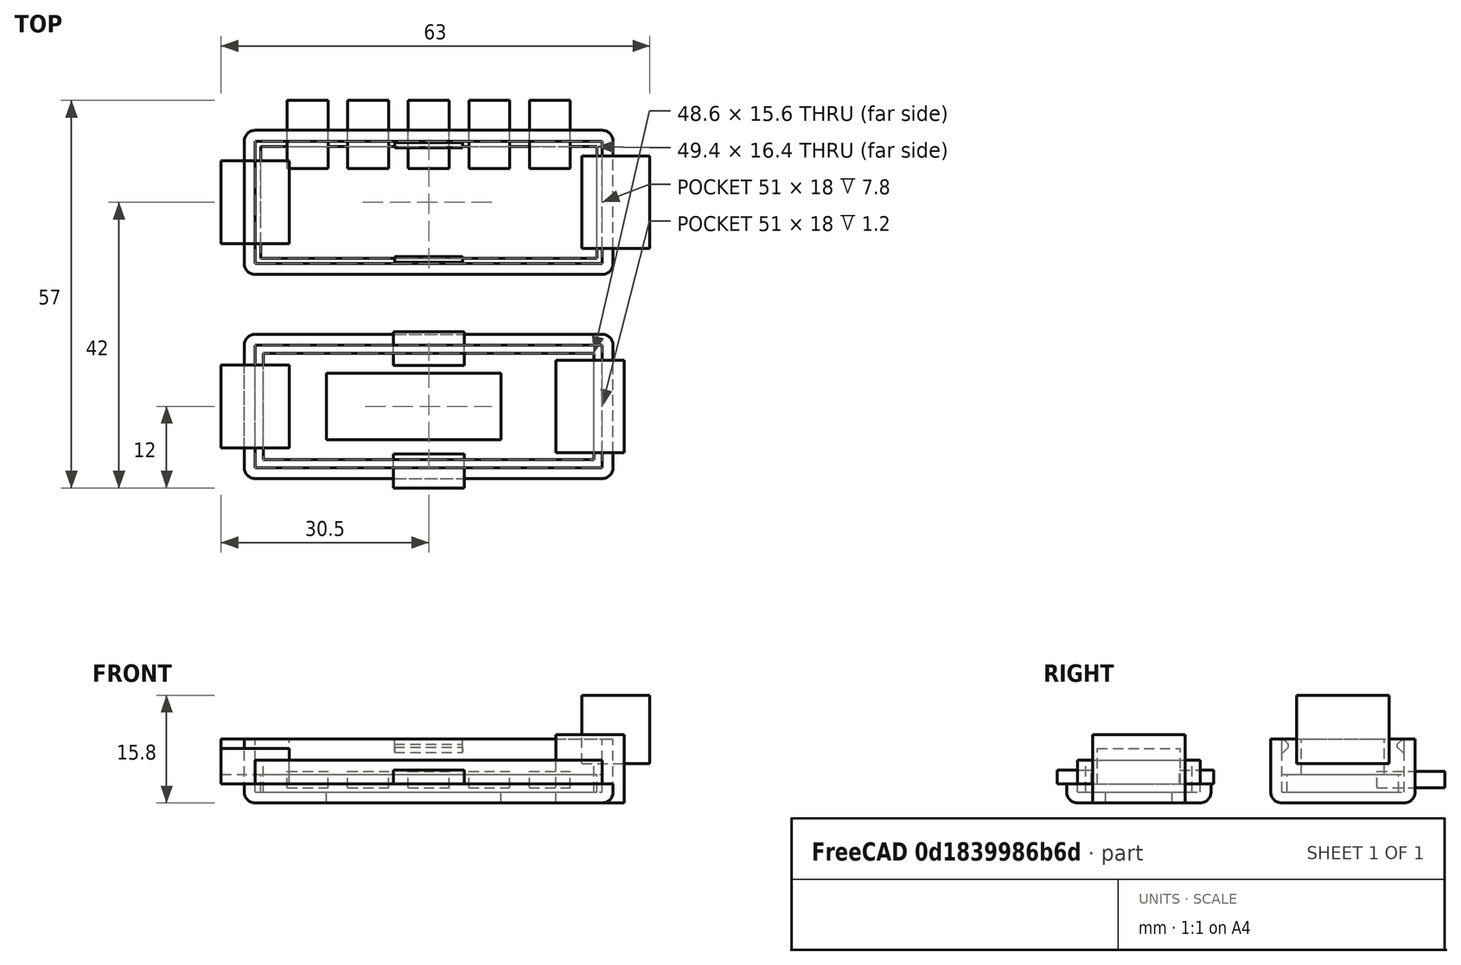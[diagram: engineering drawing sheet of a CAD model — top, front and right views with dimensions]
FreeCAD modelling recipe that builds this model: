
FCSTD DOCUMENT  (FreeCAD 0.16R)
Label: PhoneChargeGuard_raw_v0.1
License: All rights reserved
LicenseURL: http://en.wikipedia.org/wiki/All_rights_reserved
objects: Part::Box×22, Part::Cut×4, Part::Fillet×2, Part::Chamfer×2
note: 30 computed .brp shape members not serialized (recipe doc carries the construction recipe); baked Part::Feature solids carry a one-line shape summary decoded from their .brp

FEATURE [Part::Box] Box  label="unten_außen"
  Height = 9.4
  Length = 54.2
  Placement = pos=(-1.6,-1.6,0) rot=(0,0,1;0rad)
  Width = 21.2
FEATURE [Part::Box] Box001  label="unten_innen"
  Height = 9.4
  Length = 51
  Placement = pos=(0,0,1.6) rot=(0,0,1;0rad)
  Width = 18
FEATURE [Part::Cut] Cut  label="Schale_roh"
  Base = -> Box
  Tool = -> Box001
FEATURE [Part::Fillet] Fillet  label="Schale_unten"
  Base = -> Cut
  Edges = 8 edges r=1.6: [Edge1,Edge3,Edge4,Edge5,Edge6,Edge14,Edge15,Edge16]
FEATURE [Part::Box] Box002  label="Auflage_außen"
  Height = 2.6
  Length = 51
  Placement = pos=(0,0,1.6) rot=(0,0,1;0rad)
  Width = 18
FEATURE [Part::Box] Box003  label="Auflage_innen"
  Height = 2.6
  Length = 49.4
  Placement = pos=(0.8,0.8,1.6) rot=(0,0,1;0rad)
  Width = 16.4
FEATURE [Part::Cut] Cut001  label="Auflage"
  Base = -> Box002
  Tool = -> Box003
FEATURE [Part::Box] Box004  label="Haken1_roh"
  Height = 2
  Length = 10
  Placement = pos=(20.5,0,7.4) rot=(0,0,1;0rad)
  Width = 1
FEATURE [Part::Chamfer] Chamfer  label="Haken1"
  Base = -> Box004
  Edges = 2 edges r=0.8: [Edge11,Edge12]
FEATURE [Part::Box] Box005  label="Haken2_roh"
  Height = 2
  Length = 10
  Placement = pos=(20.5,17,7.4) rot=(0,0,1;0rad)
  Width = 1
FEATURE [Part::Chamfer] Chamfer001  label="Haken2"
  Base = -> Box005
  Edges = 2 edges r=0.8: [Edge9,Edge10]
FEATURE [Part::Box] Box006  label="USB_Stecker"
  Height = 5.2
  Length = 10
  Placement = pos=(-5,2.9,4.2) rot=(0,0,1;0rad)
  Width = 12.2
FEATURE [Part::Box] Box007  label="USB_Buchse"
  Height = 10
  Length = 10
  Placement = pos=(48,2.2,5.8) rot=(0,0,1;0rad)
  Width = 13.6
FEATURE [Part::Box] Box008  label="Button1"
  Height = 2.4
  Length = 6
  Placement = pos=(4.7,14,2.2) rot=(0,0,1;0rad)
  Width = 10
FEATURE [Part::Box] Box009  label="Button2"
  Height = 2.4
  Length = 6
  Placement = pos=(13.6,14,2.2) rot=(0,0,1;0rad)
  Width = 10
FEATURE [Part::Box] Box010  label="oben_außen"
  Height = 2.8
  Length = 54.2
  Placement = pos=(-1.6,-31.6,0) rot=(0,0,1;0rad)
  Width = 21.2
FEATURE [Part::Box] Box011  label="oben_innen"
  Height = 9.4
  Length = 51
  Placement = pos=(0,-30,1.6) rot=(0,0,1;0rad)
  Width = 18
FEATURE [Part::Cut] Cut002  label="Schale_oben_roh"
  Base = -> Box010
  Tool = -> Box011
FEATURE [Part::Fillet] Fillet001  label="Schale_oben"
  Base = -> Cut002
  Edges = 8 edges r=1.6: [Edge1,Edge3,Edge4,Edge5,Edge6,Edge14,Edge15,Edge16]
FEATURE [Part::Box] Box012  label="Rahmen_außen"
  Height = 4.7
  Length = 51
  Placement = pos=(0,-30,1.6) rot=(0,0,1;0rad)
  Width = 18
FEATURE [Part::Box] Box013  label="Rahmen_innen"
  Height = 4.8
  Length = 48.6
  Placement = pos=(1.2,-28.8,1.6) rot=(0,0,1;0rad)
  Width = 15.6
FEATURE [Part::Cut] Cut003  label="Rahmen"
  Base = -> Box012
  Tool = -> Box013
FEATURE [Part::Box] Box014  label="OLED"
  Height = 1.6
  Length = 25.6
  Placement = pos=(10.5,-25.9,0) rot=(0,0,1;0rad)
  Width = 9.8
FEATURE [Part::Box] Box015  label="USB_Stecker2"
  Height = 5.2
  Length = 10
  Placement = pos=(-5,-27.1,2.8) rot=(0,0,1;0rad)
  Width = 12.2
FEATURE [Part::Box] Box016  label="USB_Buchse2"
  Height = 10
  Length = 10
  Placement = pos=(44.2,-27.8,0) rot=(0,0,1;0rad)
  Width = 13.6
FEATURE [Part::Box] Box017  label="Oese1"
  Height = 2
  Length = 10.4
  Placement = pos=(20.3,-33,2.8) rot=(0,0,1;0rad)
  Width = 5
FEATURE [Part::Box] Box018  label="Oese2"
  Height = 2
  Length = 10.4
  Placement = pos=(20.3,-15,2.8) rot=(0,0,1;0rad)
  Width = 5
FEATURE [Part::Box] Box019  label="Button3"
  Height = 2.4
  Length = 6
  Placement = pos=(22.5,14,2.2) rot=(0,0,1;0rad)
  Width = 10
FEATURE [Part::Box] Box020  label="Button4"
  Height = 2.4
  Length = 6
  Placement = pos=(31.4,14,2.2) rot=(0,0,1;0rad)
  Width = 10
FEATURE [Part::Box] Box021  label="Button5"
  Height = 2.4
  Length = 6
  Placement = pos=(40.3,14,2.2) rot=(0,0,1;0rad)
  Width = 10
